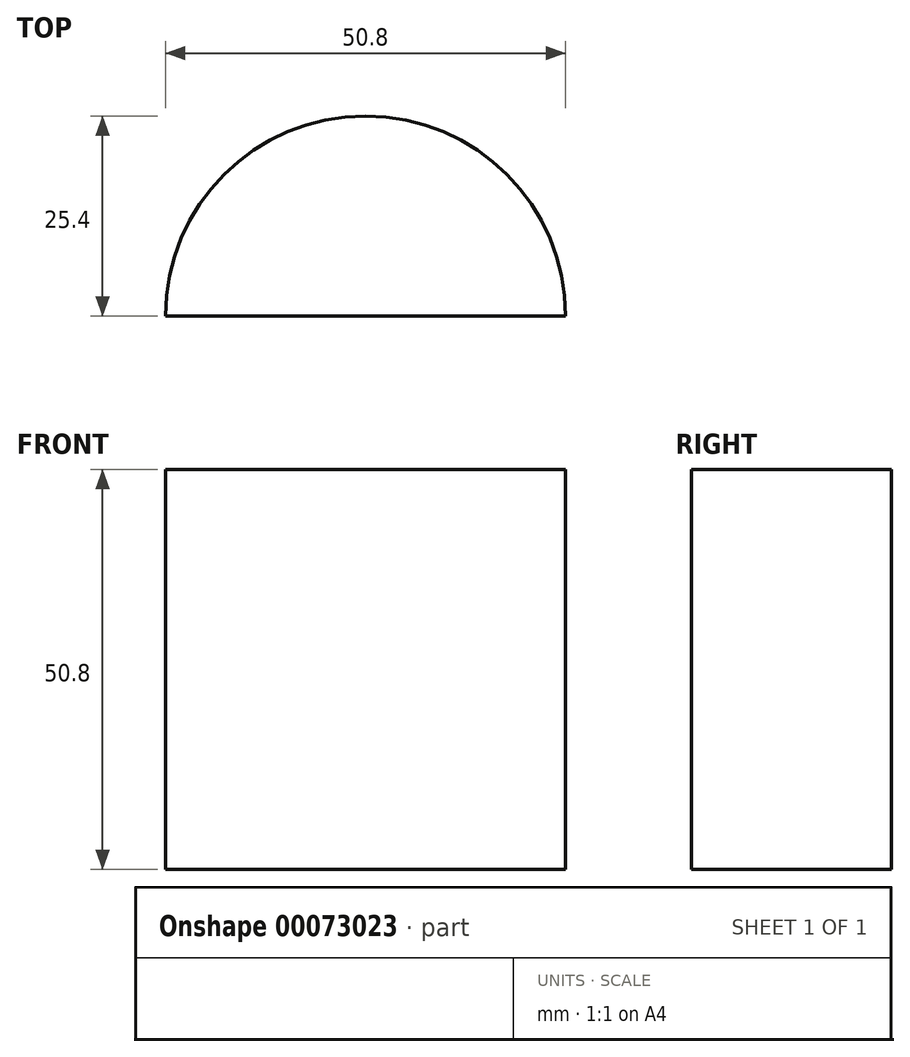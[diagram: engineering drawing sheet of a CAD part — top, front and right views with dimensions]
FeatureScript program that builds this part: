
annotation { "Feature Type Name" : "Feature", "Feature Type Description" : "" }
export const myFeature = defineFeature(function(context is Context, id is Id, definition is map)
    precondition{}
    {
        {
            var Q0;
            Q0=qCreatedBy(makeId("Top.planeOp"),FACE);
            var sketch = newSketch(context, id + "F0", { "sketchPlane" : qUnion([Q0])});
            skArc(sketch, "E0", {"start": v(25.4, 0) * mm, "mid": v(0, 25.4) * mm, "end": v(-25.4, 0) * mm});
            skLineSegment(sketch, "E1", {"start": v(-25.4, 0) * mm, "end": v(25.4, 0) * mm});
            skSolve(sketch);
        }
        {
            var Q0;
            Q0=makeQuery(id+"F0.imprint","IMPRINT",FACE,{"disambiguationData":[TD([[makeQuery(id+"F0.imprint","IMPRINT",EDGE,{"derivedFrom":sQuery(id+"F0.wireOp",EDGE,"E0")}),1.0]])]});
            extrude(context, id + "F1", {"entities" : qUnion([Q0]), "endBound" : BoundingType.SYMMETRIC, "depth" : 50.8 * mm});
        }
    });
